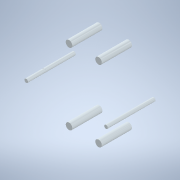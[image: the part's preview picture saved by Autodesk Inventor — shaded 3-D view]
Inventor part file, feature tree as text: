
AUTODESK INVENTOR PART (.ipt)
format: ipt  version: 2022.2 (Build 262287000, 287)  size: 120,832 bytes
history: native  units: mm
features: imported_body x6, extrude x1, sketch x1
ambient origin geometry x8: Origin, YZ Plane, XZ Plane, XY Plane, X Axis, Y Axis, Z Axis, Center Point
bodies: Solid1 (feature_tree), Solid2 (feature_tree), Solid3 (feature_tree), Solid4 (feature_tree), Solid5 (feature_tree), Solid6 (feature_tree)
feature tree (8):
  extrude  "Extrusion1"  [1 undecoded]
  sketch  "Sketch1"  dims[d0=3.0mm d1=0.0mm]
  imported_body  "Base1"
  imported_body  "Base2"
  imported_body  "Base3"
  imported_body  "Base4"
  imported_body  "Base5"
  imported_body  "Base6"
note: 1 required parameter value undecoded (feature->parameter linkage not recoverable at this tier; creation-order binding heuristic only, values carry confidence <= 0.55)
